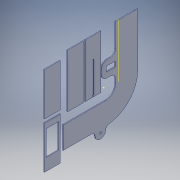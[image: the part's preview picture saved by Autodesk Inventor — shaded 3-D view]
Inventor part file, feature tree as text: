
AUTODESK INVENTOR PART (.ipt)
format: ipt  version: 2016 (Build 200138000, 138)  size: 462,336 bytes
history: native  units: in
note: dims shown in document units (in); Inventor stores cm internally (conversion verified against a paired STEP export)
features: sketch x8, extrude x6, direct_edit x2, pattern_linear x2, fillet x2, move_body x2
ambient origin geometry x8: Origin, YZ Plane, XZ Plane, XY Plane, X Axis, Y Axis, Z Axis, Center Point
bodies: Solid1 (feature_tree)
feature tree (22):
  sketch  "Sketch1"  dims[d0=0.0591in d1=0.0in d2=0.1181in d3=0.0in]
  extrude  "Extrusion1"  Depth=0.1181in TaperAngle=0.0deg
  extrude  "Extrusion2"  TaperAngle=0.0deg  [1 undecoded]
  direct_edit  "Direct Edit1"
  direct_edit  "Direct Edit2"
  sketch  "Sketch4"  dims[d12=0.0787in d13=0.0in d14=0.7874in d16=1.9291in]
  extrude  "Extrusion3"  Depth=1.752in
  pattern_linear  "Rectangular Pattern1"  Count1=2 Spacing1=1.9291in
  extrude  "Extrusion4"  Depth=0.1969in
  fillet  "Fillet1"  [1 undecoded]
  extrude  "Extrusion5"  Depth=0.0787in
  pattern_linear  "Rectangular Pattern2"  Count1=12  [1 undecoded]
  extrude  "Extrusion6"  Depth=0.0787in TaperAngle=0.0deg
  sketch  "Sketch2"  dims[d4=0.0in d5=0.0in d6=-0.0394in d7=0.0in d8=0.0in d9=-0.0197in]
  sketch  "Sketch3"  dims[d10=5.9055in d11=1.752in]
  sketch  "Sketch5"  dims[d17=3.5433in d18=0.1969in d19=0.0in d20=0.0in]
  sketch  "Sketch6"  dims[d21=0.0984in d22=0.0787in]
  sketch  "Sketch7"  dims[d23=1.752in d24=4.7244in]
  sketch  "Sketch8"  dims[d25=0.3937in d26=0.0787in d27=0.0in d28=0.7874in d30=5.1181in d31=1.378in d32=2.7559in d33=0.6299in d34=0.0787in d35=0.0in]
  fillet  "Fillet2"  Radius=0.7874in
  move_body  "Move1"
  move_body  "Move2"
note: 3 required parameter values undecoded (feature->parameter linkage not recoverable at this tier; creation-order binding heuristic only, values carry confidence <= 0.55)
